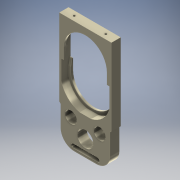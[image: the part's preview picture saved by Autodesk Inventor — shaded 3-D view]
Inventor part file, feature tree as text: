
AUTODESK INVENTOR PART (.ipt)
format: ipt  version: 2016 (Build 200138000, 138)  size: 317,952 bytes
history: native  units: mm
features: extrude x10, sketch x9, chamfer x6, projected_geometry x5, mirror x2, hole x1, thicken_offset x1, reference x1
ambient origin geometry x8: Origin, YZ Plane, XZ Plane, XY Plane, X Axis, Y Axis, Z Axis, Center Point
bodies: Body1 (feature_tree)
feature tree (35):
  sketch  "Sketch13"  dims[d49=70.0mm d50=62.75mm]
  extrude  "Extrusion11"  Depth=62.75mm
  extrude  "Extrusion12"  Depth=62.75mm
  extrude  "Extrusion13"  Depth=111.0mm
  chamfer  "Chamfer3"  Distance=3.0mm
  chamfer  "Chamfer4"  Distance=10.5mm
  chamfer  "Chamfer5"  Distance=3.0mm
  chamfer  "Chamfer6"  Distance=2.0mm Angle=45.0deg
  chamfer  "Chamfer7"  Distance=10.0mm Angle=45.0deg
  extrude  "Extrusion17"  Depth=2.0mm TaperAngle=45.0deg
  mirror  "Mirror4"
  extrude  "Extrusion14"  Depth=3.0mm TaperAngle=0.0deg
  sketch  "Sketch16"  dims[d68=10.0mm d69=2.0mm d70=45.0deg d71=2.0mm d72=10.0mm d73=45.0deg]
  extrude  "Extrusion20"  Depth=3.0mm
  extrude  "Extrusion21"  Depth=50.0mm TaperAngle=0.0deg
  chamfer  "Chamfer8"  Distance=3.0mm
  extrude  "Extrusion22"  Depth=20.0mm
  extrude  "Extrusion23"  Depth=6.0mm TaperAngle=0.0deg
  mirror  "Mirror5"
  hole  "Hole1"  [1 undecoded]
  extrude  "Extrusion24"  Depth=72.0mm
  thicken_offset  "Thicken2"
  sketch  "Sketch14"  dims[d51=70.0mm d53=62.75mm]
  projected_geometry  "Projected Loop2"
  sketch  "Sketch15"  dims[d54=76.0mm d55=111.0mm d56=3.0mm d57=0.0mm d58=10.5mm d59=0.0mm d60=3.0mm d61=0.0mm d62=2.0mm d63=2.0mm d64=45.0deg d65=10.0mm d66=2.0mm d67=45.0deg]
  projected_geometry  "Projected Loop3"
  sketch  "Sketch21"  dims[d74=2.0mm d75=10.0mm d76=45.0deg d77=3.0mm d78=0.0mm]
  projected_geometry  "Projected Loop5"
  sketch  "Sketch22"  dims[d85=45.0deg d86=3.0mm]
  sketch  "Sketch23"  dims[d87=50.0mm d88=0.0mm d95=50.0mm d96=0.0mm]
  projected_geometry  "Projected Loop6"
  sketch  "Sketch24"  dims[d97=35.0mm]
  projected_geometry  "Projected Loop7"
  reference  "Reference20"
  sketch  "Sketch25"  dims[d98=3.0mm d99=3.0mm d100=20.0mm d101=6.0mm d102=0.0mm d103=1.0mm d104=2.0mm d105=45.0deg d108=72.0mm d109=10.0mm d110=0.0mm d111=72.0mm d112=10.0mm d113=0.0mm d115=3.0mm d116=6.0mm d117=4.0mm d118=2.0mm d119=90.0deg d120=8.0mm d121=20.594885mm d122=0.2mm d123=0.15mm d124=10.0mm d125=0.0mm]
note: 1 required parameter value undecoded (feature->parameter linkage not recoverable at this tier; creation-order binding heuristic only, values carry confidence <= 0.55)
